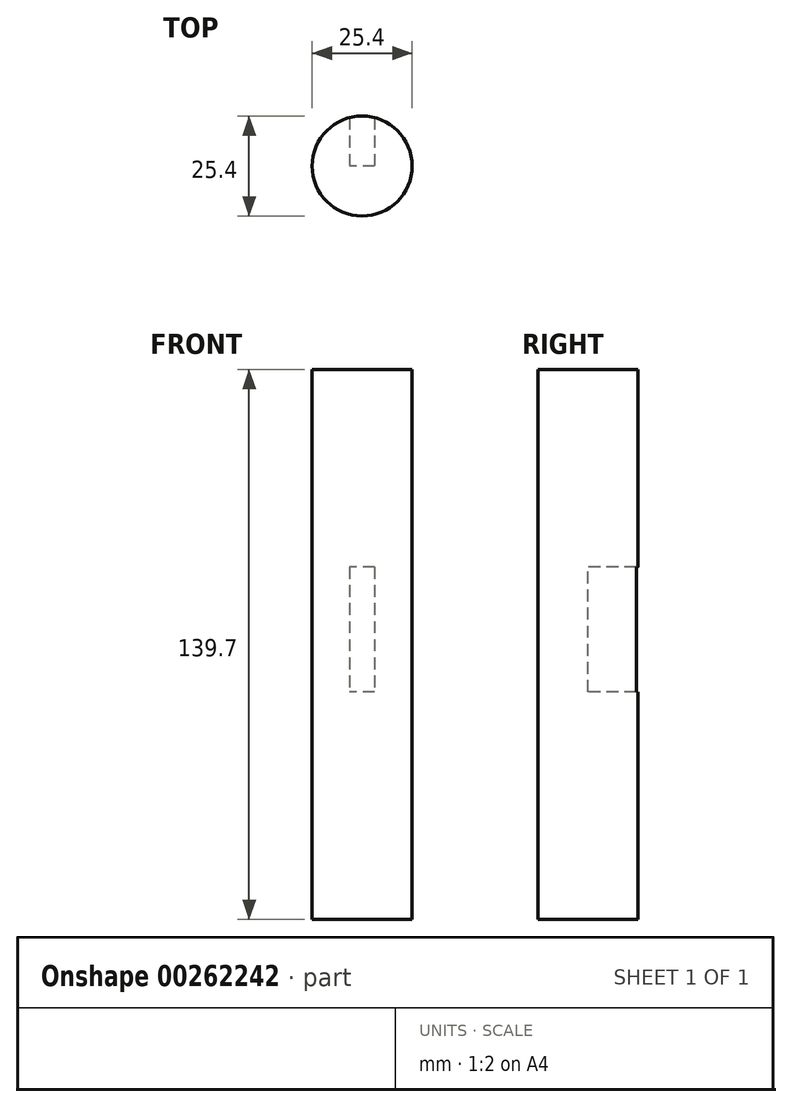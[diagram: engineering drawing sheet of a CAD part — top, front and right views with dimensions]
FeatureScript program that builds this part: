
annotation { "Feature Type Name" : "Feature", "Feature Type Description" : "" }
export const myFeature = defineFeature(function(context is Context, id is Id, definition is map)
    precondition{}
    {
        {
            var Q0;
            Q0=qCreatedBy(makeId("Top.planeOp"),FACE);
            var sketch = newSketch(context, id + "F0", { "sketchPlane" : qUnion([Q0])});
            skCircle(sketch, "E0", {"center": v(0, 0) * mm, "radius": 12.7 * mm});
            skPoint(sketch, "E1.middle", {"position": v(-12.7, 0) * mm});
            skSolve(sketch);
        }
        {
            var Q0;
            Q0=makeQuery(id+"F0.imprint","IMPRINT",FACE,{"disambiguationData":[TD([[makeQuery(id+"F0.imprint","IMPRINT",EDGE,{"derivedFrom":sQuery(id+"F0.wireOp",EDGE,"E0")}),1.0]])]});
            extrude(context, id + "F1", {"entities" : qUnion([Q0]), "depth" : 139.7 * mm});
        }
        {
            var Q0;
            Q0=qCreatedBy(makeId("Front.planeOp"),FACE);
            var sketch = newSketch(context, id + "F2", { "sketchPlane" : qUnion([Q0])});
            skLineSegment(sketch, "E2.bottom", {"start": v(3.17, 57.8) * mm, "end": v(-3.18, 57.8) * mm});
            skLineSegment(sketch, "E2.top", {"start": v(3.18, 89.55) * mm, "end": v(-3.18, 89.55) * mm});
            skLineSegment(sketch, "E2.left", {"start": v(3.17, 57.8) * mm, "end": v(3.18, 89.55) * mm});
            skLineSegment(sketch, "E2.right", {"start": v(-3.18, 57.8) * mm, "end": v(-3.18, 89.55) * mm});
            skPoint(sketch, "E2.middle", {"position": v(0, 73.68) * mm});
            skSolve(sketch);
        }
        {
            var Q0;
            Q0 = qSketchRegion(id + "F2", true);
            extrude(context, id + "F3", {"entities" : qUnion([Q0]), "operationType" : NewBodyOperationType.REMOVE, "oppositeDirection" : true, "depth" : 30.73 * mm});
        }
    });
